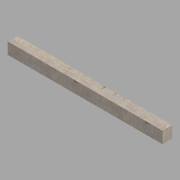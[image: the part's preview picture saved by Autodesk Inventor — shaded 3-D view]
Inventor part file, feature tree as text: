
AUTODESK INVENTOR PART (.ipt)
format: ipt  version: 2022.1 (Build 261234020, 234B)  size: 136,704 bytes
history: native  units: in
note: dims shown in document units (in); Inventor stores cm internally (conversion verified against a paired STEP export)
features: extrude x2, sketch x2, other x1
ambient origin geometry x8: Origin, YZ Plane, XZ Plane, XY Plane, X Axis, Y Axis, Z Axis, Center Point
bodies: Body1 (feature_tree)
feature tree (5):
  other  "Sawn bridge veneer"
  extrude  "Extrusion1"  Depth=3.0in
  extrude  "Extrusion2"  Depth=3.625in
  sketch  "Sketch1"  dims[d0=48.0in d1=3.0in]
  sketch  "Sketch2"  dims[d2=3.625in d3=0.0in d4=0.375in d5=0.25in d6=0.25in d7=0.25in d8=0.25in d9=0.3958in d10=0.25in d11=0.25in d12=0.3958in d13=0.3958in d14=0.25in d15=0.25in d16=0.25in d17=0.25in d18=0.3958in d19=0.3958in d20=0.396in d21=0.0in d22=0.0in]
